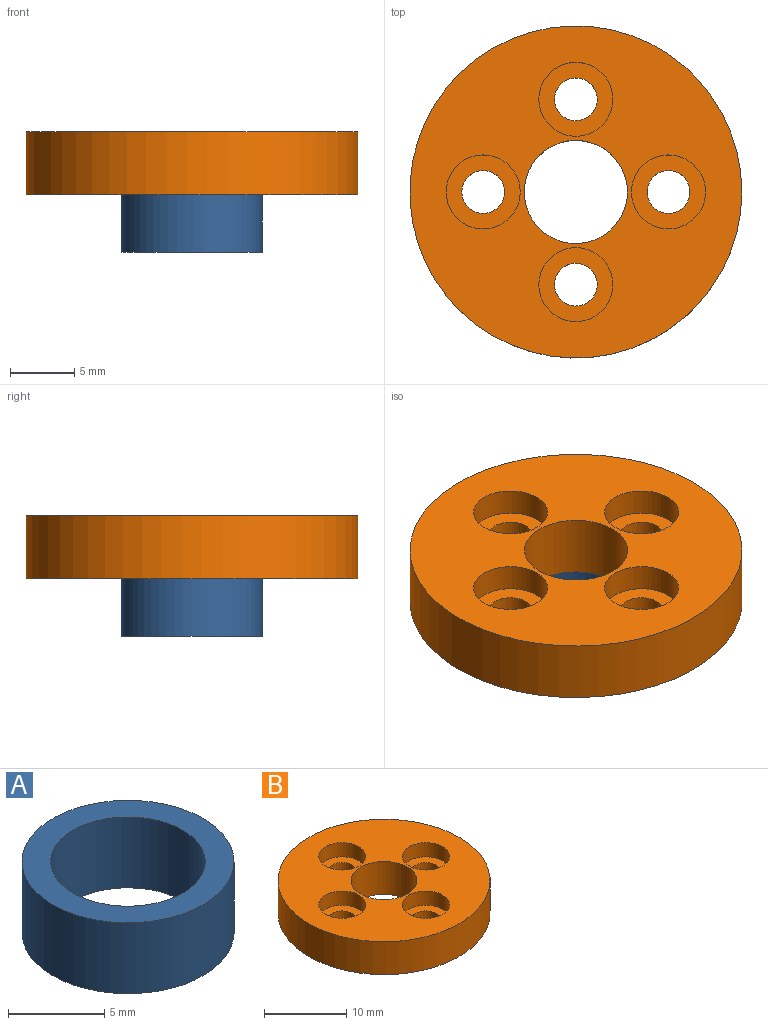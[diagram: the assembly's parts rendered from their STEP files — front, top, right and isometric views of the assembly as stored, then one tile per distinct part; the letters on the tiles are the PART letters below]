
ASSEMBLY  parts=2 mates=1
PART A: 4 faces, bbox 11x11x4.5 mm
  f0: cylinder r=4.01mm len=8.02mm, axis (0,0,1), area 113.3mm2, adj f2,f3
  f1: cylinder r=5.5mm len=11mm, axis (0,0,1), area 155.5mm2, adj f2,f3
  f2: plane 11x11mm, normal (0,0,-1), area 44.6mm2, adj f0,f1
  f3: plane 11x11mm, normal (0,0,1), area 44.6mm2, adj f0,f1
PART B: 16 faces, bbox 25.8x25.8x4.9 mm
  f0: cylinder r=1.66mm len=3.32mm, axis (0,0,1), area 29.2mm2, adj f6,f9
  f1: cylinder r=1.66mm len=3.32mm, axis (0,0,1), area 29.2mm2, adj f6,f13
  f2: cylinder r=1.66mm len=3.32mm, axis (0,0,1), area 29.2mm2, adj f6,f15
  f3: cylinder r=1.66mm len=3.32mm, axis (0,0,1), area 29.2mm2, adj f6,f11
  f4: cylinder r=12.9mm len=25.8mm, axis (0,0,1), area 397.2mm2, adj f6,f7
  f5: cylinder r=4.01mm len=8.02mm, axis (0,0,1), area 123.4mm2, adj f6,f7
  f6: plane 25.8x25.8mm, normal (0,0,-1), area 437.7mm2, adj f0,f1,f2,f3,f4,f5
  f7: plane 25.8x25.8mm, normal (0,0,1), area 368.5mm2, adj f4,f5,f8,f10,f12,f14
  f8: cylinder r=2.88mm len=5.75mm, axis (0,0,1), area 37.9mm2, adj f7,f9
  f9: plane 5.75x5.75mm, normal (0,0,1), area 17.3mm2, adj f0,f8
  f10: cylinder r=2.88mm len=5.75mm, axis (0,0,1), area 37.9mm2, adj f7,f11
  f11: plane 5.75x5.75mm, normal (0,0,1), area 17.3mm2, adj f3,f10
  f12: cylinder r=2.88mm len=5.75mm, axis (0,0,1), area 37.9mm2, adj f7,f13
  f13: plane 5.75x5.75mm, normal (0,0,1), area 17.3mm2, adj f1,f12
  f14: cylinder r=2.88mm len=5.75mm, axis (0,0,1), area 37.9mm2, adj f7,f15
  f15: plane 5.75x5.75mm, normal (0,0,1), area 17.3mm2, adj f2,f14
PLACE A t=(-5.2,-6.97,0.59)mm
PLACE B t=(-5.2,-6.97,0.59)mm
MATE fastened A.f0 <-> B.f5  axis (0,0,1) through (-5.2,-6.97,-4.31)mm
